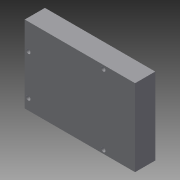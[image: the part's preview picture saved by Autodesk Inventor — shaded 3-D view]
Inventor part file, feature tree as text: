
AUTODESK INVENTOR PART (.ipt)
format: ipt  version: 2013 (Build 170138000, 138)  size: 87,040 bytes
history: native  units: mm
features: extrude x1, sketch x1
ambient origin geometry x8: Origin, YZ Plane, XZ Plane, XY Plane, X Axis, Y Axis, Z Axis, Center Point
bodies: Solid1 (feature_tree)
feature tree (2):
  extrude  "Extrusion1"  Depth=76.5mm
  sketch  "Sketch1"  dims[d0=53.4mm d2=76.5mm d3=3.0mm d4=3.0mm d5=3.0mm d6=3.0mm d7=2.5mm d8=7.5mm d9=28.0mm d10=2.5mm d11=52.0mm d12=2.5mm d13=52.0mm d14=14.0mm d15=0.0mm d16=2.5mm]
